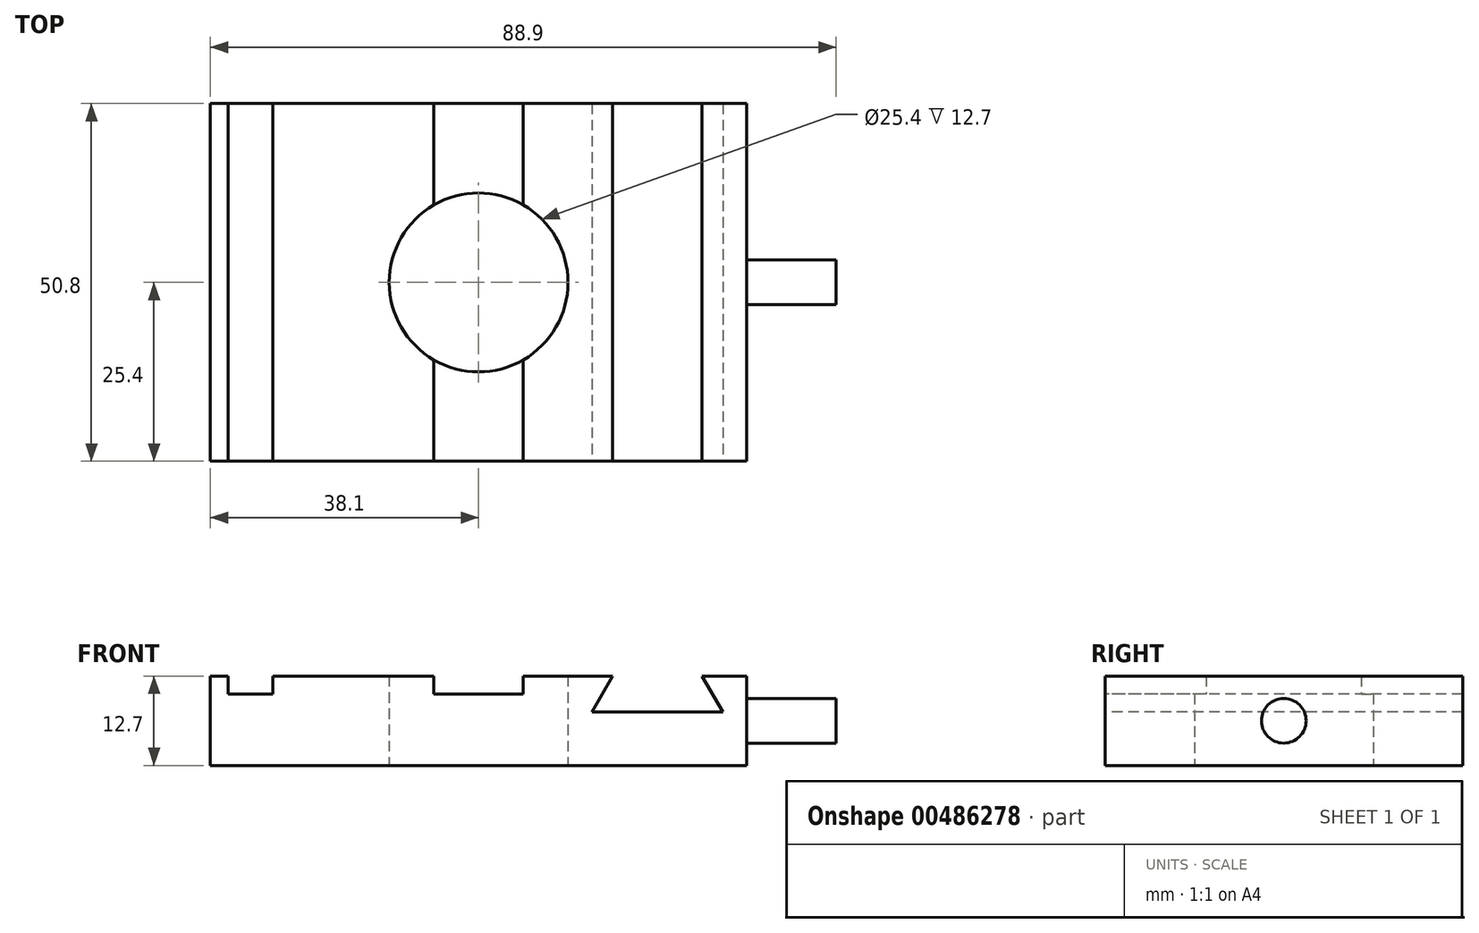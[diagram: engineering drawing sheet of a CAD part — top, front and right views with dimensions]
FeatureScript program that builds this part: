
annotation { "Feature Type Name" : "Feature", "Feature Type Description" : "" }
export const myFeature = defineFeature(function(context is Context, id is Id, definition is map)
    precondition{}
    {
        {
            var Q0;
            Q0=qCreatedBy(makeId("Top.planeOp"),FACE);
            var sketch = newSketch(context, id + "F0", { "sketchPlane" : qUnion([Q0])});
            skLineSegment(sketch, "E0.bottom", {"start": v(38.1, -25.4) * mm, "end": v(-38.1, -25.4) * mm});
            skLineSegment(sketch, "E0.top", {"start": v(38.1, 25.4) * mm, "end": v(-38.1, 25.4) * mm});
            skLineSegment(sketch, "E0.left", {"start": v(38.1, -25.4) * mm, "end": v(38.1, 25.4) * mm});
            skLineSegment(sketch, "E0.right", {"start": v(-38.1, -25.4) * mm, "end": v(-38.1, 25.4) * mm});
            skPoint(sketch, "E0.middle", {"position": v(0, 0) * mm});
            skCircle(sketch, "E1", {"center": v(0, 0) * mm, "radius": 12.7 * mm});
            skSolve(sketch);
        }
        {
            var Q0;
            Q0=makeQuery(id+"F0.imprint","IMPRINT",FACE,{"disambiguationData":[TD([[makeQuery(id+"F0.imprint","IMPRINT",EDGE,{"derivedFrom":sQuery(id+"F0.wireOp",EDGE,"E0.bottom")}),-1.0]])]});
            extrude(context, id + "F1", {"entities" : qUnion([Q0]), "depth" : 12.7 * mm, "offsetDistance" : 25.4 * mm});
        }
        {
            var Q0;
            Q0=makeQuery(id+"F1.opExtrude","CAP_FACE",FACE,{"disambiguationData":[OSD([sQuery(id+"F0.wireOp",EDGE,"E0.bottom"),sQuery(id+"F0.wireOp",EDGE,"E0.top"),sQuery(id+"F0.wireOp",EDGE,"E0.left"),sQuery(id+"F0.wireOp",EDGE,"E0.right"),sQuery(id+"F0.wireOp",EDGE,"E1")])],"isStart":false});
            var sketch = newSketch(context, id + "F2", { "sketchPlane" : qUnion([Q0])});
            skLineSegment(sketch, "E2", {"start": v(-35.56, 25.4) * mm, "end": v(-35.56, -25.4) * mm});
            skLineSegment(sketch, "E3", {"start": v(-29.2, -25.4) * mm, "end": v(-29.21, 25.4) * mm});
            skLineSegment(sketch, "E4.bottom", {"start": v(-6.35, 25.4) * mm, "end": v(6.35, 25.4) * mm});
            skLineSegment(sketch, "E4.top", {"start": v(-6.35, -25.4) * mm, "end": v(6.35, -25.4) * mm});
            skLineSegment(sketch, "E4.left", {"start": v(-6.35, 25.4) * mm, "end": v(-6.35, -25.4) * mm});
            skLineSegment(sketch, "E4.right", {"start": v(6.35, 25.4) * mm, "end": v(6.35, -25.4) * mm});
            skPoint(sketch, "E5", {"position": v(0, 0) * mm});
            skLineSegment(sketch, "E6", {"start": v(0, 25.4) * mm, "end": v(0, -25.4) * mm, "construction": true});
            skSolve(sketch);
        }
        {
            var Q0;
            {var subQ0=sQuery(id+"F2.wireOp",EDGE,"E4.left");var subQ1=makeQuery(id+"F1.opExtrude","CAP_EDGE",EDGE,{"disambiguationData":[OSD([sQuery(id+"F0.wireOp",EDGE,"E1")])],"isStart":false});var subQ2=makeQuery(id+"F2.imprint","INTERSECT",VERTEX,{"disambiguationData":[OD(0.0)],"derivedFrom":[subQ1,subQ0]});Q0=makeQuery(id+"F2.imprint","IMPRINT",FACE,{"disambiguationData":[TD([[makeQuery(id+"F2.imprint","IMPRINT",EDGE,{"disambiguationData":[TD([[subQ2,-1.0]])],"derivedFrom":subQ0}),1.0]])]});}
            var Q1;
            {var subQ0=sQuery(id+"F2.wireOp",EDGE,"E2");Q1=makeQuery(id+"F2.imprint","IMPRINT",FACE,{"disambiguationData":[TD([[makeQuery(id+"F2.imprint","IMPRINT",EDGE,{"derivedFrom":subQ0}),1.0]])]});}
            var Q2;
            {var subQ0=sQuery(id+"F2.wireOp",EDGE,"E4.top");Q2=makeQuery(id+"F2.imprint","IMPRINT",FACE,{"disambiguationData":[TD([[makeQuery(id+"F2.imprint","IMPRINT",EDGE,{"derivedFrom":subQ0}),-1.0]])]});}
            var Q3;
            {var subQ0=sQuery(id+"F2.wireOp",EDGE,"E4.bottom");Q3=makeQuery(id+"F2.imprint","IMPRINT",FACE,{"disambiguationData":[TD([[makeQuery(id+"F2.imprint","IMPRINT",EDGE,{"derivedFrom":subQ0}),1.0]])]});}
            extrude(context, id + "F3", {"entities" : qUnion([Q0, Q1, Q2, Q3]), "operationType" : NewBodyOperationType.REMOVE, "oppositeDirection" : true, "depth" : 2.54 * mm, "offsetDistance" : 25.4 * mm});
        }
        {
            var Q0;
            Q0=makeQuery(id+"F1.opExtrude","SWEPT_FACE",FACE,{"disambiguationData":[OSD([sQuery(id+"F0.wireOp",EDGE,"E0.bottom")])]});
            var sketch = newSketch(context, id + "F4", { "sketchPlane" : qUnion([Q0])});
            skLineSegment(sketch, "E7", {"start": v(19.05, 12.7) * mm, "end": v(16.12, 7.62) * mm});
            skLineSegment(sketch, "E8", {"start": v(16.12, 7.62) * mm, "end": v(34.68, 7.62) * mm});
            skLineSegment(sketch, "E9", {"start": v(34.68, 7.62) * mm, "end": v(31.75, 12.7) * mm});
            skLineSegment(sketch, "E10", {"start": v(31.75, 12.7) * mm, "end": v(19.05, 12.7) * mm});
            skLineSegment(sketch, "E11", {"start": v(25.4, 12.7) * mm, "end": v(25.4, 7.62) * mm, "construction": true});
            skSolve(sketch);
        }
        {
            var Q0;
            Q0=makeQuery(id+"F4.imprint","IMPRINT",FACE,{"disambiguationData":[TD([[makeQuery(id+"F4.imprint","IMPRINT",EDGE,{"derivedFrom":sQuery(id+"F4.wireOp",EDGE,"E7")}),1.0]])]});
            extrude(context, id + "F5", {"entities" : qUnion([Q0]), "operationType" : NewBodyOperationType.REMOVE, "endBound" : BoundingType.UP_TO_NEXT, "oppositeDirection" : true, "depth" : 25.4 * mm, "offsetDistance" : 25.4 * mm});
        }
        {
            var Q0;
            Q0=makeQuery(id+"F1.opExtrude","SWEPT_FACE",FACE,{"disambiguationData":[OSD([sQuery(id+"F0.wireOp",EDGE,"E0.left")])]});
            var sketch = newSketch(context, id + "F6", { "sketchPlane" : qUnion([Q0])});
            skCircle(sketch, "E12", {"center": v(0, 6.35) * mm, "radius": 3.18 * mm});
            skPoint(sketch, "E12.centerSnap0", {"position": v(25.4, 6.35) * mm});
            skPoint(sketch, "E12.centerSnap1", {"position": v(0, 0) * mm});
            skSolve(sketch);
        }
        {
            var Q0;
            Q0=makeQuery(id+"F6.imprint","IMPRINT",FACE,{"disambiguationData":[TD([[makeQuery(id+"F6.imprint","IMPRINT",EDGE,{"derivedFrom":sQuery(id+"F6.wireOp",EDGE,"E12")}),1.0]])]});
            extrude(context, id + "F7", {"entities" : qUnion([Q0]), "operationType" : NewBodyOperationType.ADD, "depth" : 12.7 * mm, "offsetDistance" : 25.4 * mm});
        }
    });
